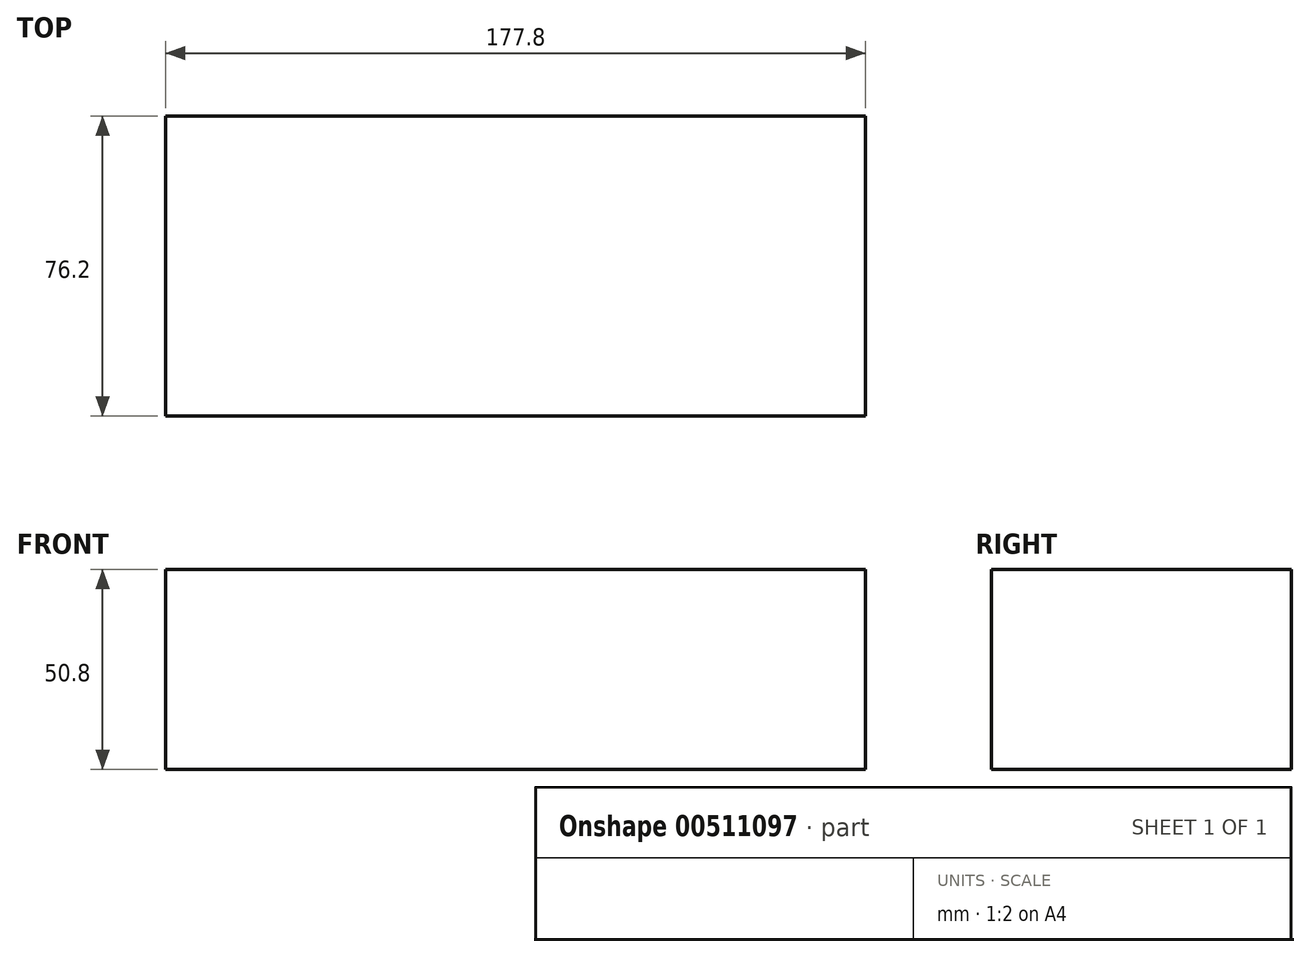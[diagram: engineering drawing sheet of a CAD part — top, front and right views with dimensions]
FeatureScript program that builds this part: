
annotation { "Feature Type Name" : "Feature", "Feature Type Description" : "" }
export const myFeature = defineFeature(function(context is Context, id is Id, definition is map)
    precondition{}
    {
        {
            var Q0;
            Q0=qCreatedBy(makeId("Front.planeOp"),FACE);
            var sketch = newSketch(context, id + "F0", { "sketchPlane" : qUnion([Q0])});
            skLineSegment(sketch, "E0.bottom", {"start": v(-95.45, 1.04) * mm, "end": v(82.35, 1.04) * mm});
            skLineSegment(sketch, "E0.top", {"start": v(-95.45, -49.76) * mm, "end": v(82.35, -49.76) * mm});
            skLineSegment(sketch, "E0.left", {"start": v(-95.45, 1.04) * mm, "end": v(-95.45, -49.76) * mm});
            skLineSegment(sketch, "E0.right", {"start": v(82.35, 1.04) * mm, "end": v(82.35, -49.76) * mm});
            skSolve(sketch);
        }
        {
            var Q0;
            Q0=makeQuery(id+"F0.imprint","IMPRINT",FACE,{"disambiguationData":[TD([[makeQuery(id+"F0.imprint","IMPRINT",EDGE,{"derivedFrom":sQuery(id+"F0.wireOp",EDGE,"E0.bottom")}),-1.0]])]});
            extrude(context, id + "F1", {"entities" : qUnion([Q0]), "depth" : 76.2 * mm});
        }
    });
